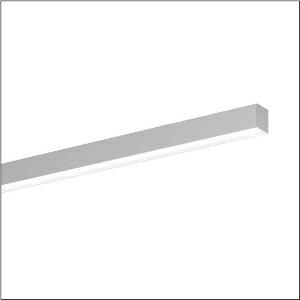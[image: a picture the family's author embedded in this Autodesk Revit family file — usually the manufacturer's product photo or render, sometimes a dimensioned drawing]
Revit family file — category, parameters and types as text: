
# Revit family: silica_r__21_51mx23da34sb_798d
name_source: partatom
category: Lighting Fixtures
units: mm (PartAtom-declared; Revit-internal decimal feet)

## family parameters
Cut with Voids When Loaded = No
Host = Face
Light Source = No
Part Type = Normal
Room Calculation Point = No
Round Connector Dimension = Use Diameter
Shared = No

## types (1)
- --- (1 x LED, 3280 lm, 24.1 W, 3000K)
    Apparent Load = 24 VA
    CIE Flux Codes = 78 96 99 100 100
    Color Rendering = 80
    Color Temperature = 3000K
    Default Elevation = 1800 mm
    Description = Silica® 21, office luminaire, primary optical cover: prismatic diffuser, of PMMA, CAT 2 (L<= 3000cd/m²), light emission: direct distribution, primary light characteristic: symmetric, installation type: surface-mounted, LED, rated luminous flux: 3.280lm, luminous efficacy: 136lm/W, light colour: 830, colour temperature: 3000K, with terminal, 3+2-pole, max. 2.5mm², mains connection: 220..240V, AC, 50/60Hz, rated input power: 24.1W, luminaire housing, of aluminium, metallic grey (RAL 9006), length: 1.204mm, width: 53mm, height: 53mm, protection rating (complete): IP20, insulation class (complete): insulation class I (protective earthing), certification: CE, permissible operating ambient temperature: 0..+35°C, standard: EN 50419, packaging unit: 1 piece
    Height = 0 mm  [stored 0 ft]
    Lamp = 1 x LED
    Lamp Light Flux = 3280 lm
    Lamp Power = 24.1 W
    Lamp count = 1
    Length = 1204 mm
    Luminous efficacy = 136 lm/W
    Manufacturer = Siteco
    ModVariant = No
    Model = 51MX23DA34SB
    Mounting Place = Ceiling
    Mounting Type = Recessed
    Number of Poles = 1
    OnlyDefault = Yes
    Power Factor = 1
    Product Name = Silica® 21
    Product group = office luminaire | ceiling recessed
    ProductGroupID = 401
    Protection Class = Protection class I
    Protection Degree = IP 20
    RLX_Detail_Level = 1
    RLX_Emergency_Light_Flux = 0 lm
    RLX_Emergency_Type = 0
    RLX_Emergency_Type_DB = No
    RlxData = <blob elided: 21285 chars, md5=7bd7e0d3>
    Socket = socket
    Standby Power = 0 W
    System Light Flux = 3280 lm
    System Power = 24 W
    Type Comments = factory setting: luminous flux: 100 % | dim-lin: 254 | 345 mA
    Type Image = l_1313588.jpg
    URL = http://relux.com
    VarID = @adj_067897
    Voltage = 0 V
    Weight = 0.00 kg
    Width = 53 mm

note: [stored X ft] marks values corroborated as IEEE doubles in the binary element streams (Revit-internal decimal feet)

## geometry (parser evidence)
native form markers: Blend x4, Sweep x12
no freeform markers — native parametric forms only
